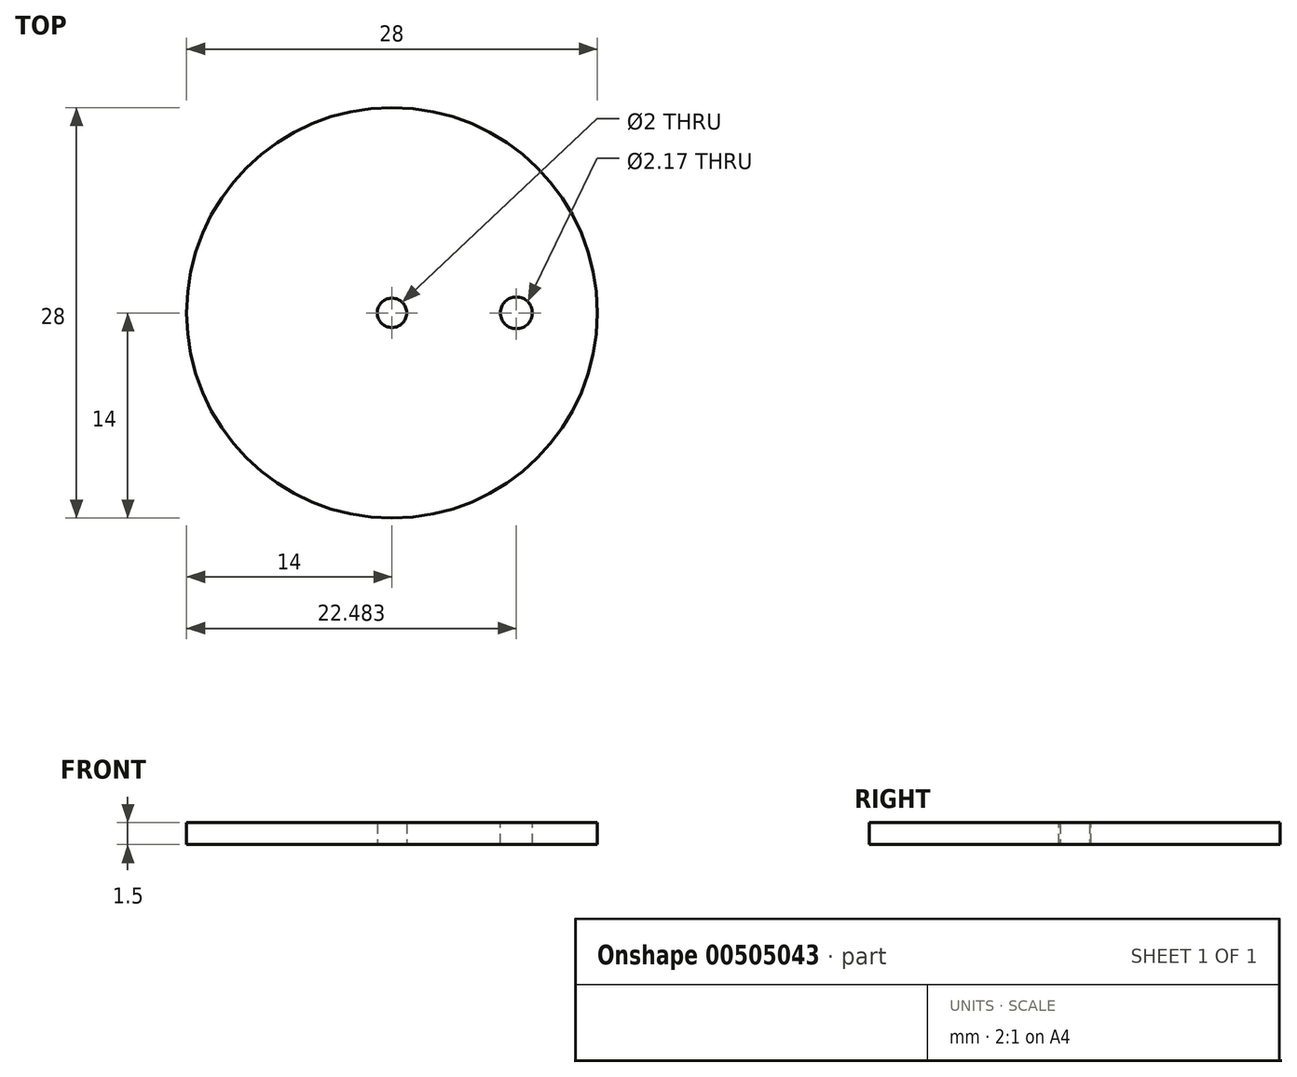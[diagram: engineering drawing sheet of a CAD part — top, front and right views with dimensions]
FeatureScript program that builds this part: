
annotation { "Feature Type Name" : "Feature", "Feature Type Description" : "" }
export const myFeature = defineFeature(function(context is Context, id is Id, definition is map)
    precondition{}
    {
        {
            var Q0;
            Q0=qCreatedBy(makeId("Top.planeOp"),FACE);
            var sketch = newSketch(context, id + "F0", { "sketchPlane" : qUnion([Q0])});
            skCircle(sketch, "E0", {"center": v(0, 0) * mm, "radius": 1 * mm});
            skCircle(sketch, "E1", {"center": v(0, 0) * mm, "radius": 14 * mm});
            skSolve(sketch);
        }
        {
            var Q0;
            Q0=makeQuery(id+"F0.imprint","IMPRINT",FACE,{"disambiguationData":[TD([[makeQuery(id+"F0.imprint","IMPRINT",EDGE,{"derivedFrom":sQuery(id+"F0.wireOp",EDGE,"E0")}),-1.0]])]});
            extrude(context, id + "F1", {"entities" : qUnion([Q0]), "depth" : 1.5 * mm});
        }
        {
            var Q0;
            Q0=makeQuery(id+"F1.opExtrude","CAP_FACE",FACE,{"disambiguationData":[OSD([sQuery(id+"F0.wireOp",EDGE,"E0"),sQuery(id+"F0.wireOp",EDGE,"E1")])],"isStart":false});
            var sketch = newSketch(context, id + "F2", { "sketchPlane" : qUnion([Q0])});
            skCircle(sketch, "E2", {"center": v(8.48, 0) * mm, "radius": 1.08 * mm});
            skSolve(sketch);
        }
        {
            var Q0;
            Q0=makeQuery(id+"F2.imprint","IMPRINT",FACE,{"disambiguationData":[TD([[makeQuery(id+"F2.imprint","IMPRINT",EDGE,{"derivedFrom":sQuery(id+"F2.wireOp",EDGE,"E2")}),1.0]])]});
            extrude(context, id + "F3", {"entities" : qUnion([Q0]), "operationType" : NewBodyOperationType.REMOVE, "endBound" : BoundingType.UP_TO_NEXT, "oppositeDirection" : true, "depth" : 25 * mm});
        }
    });
